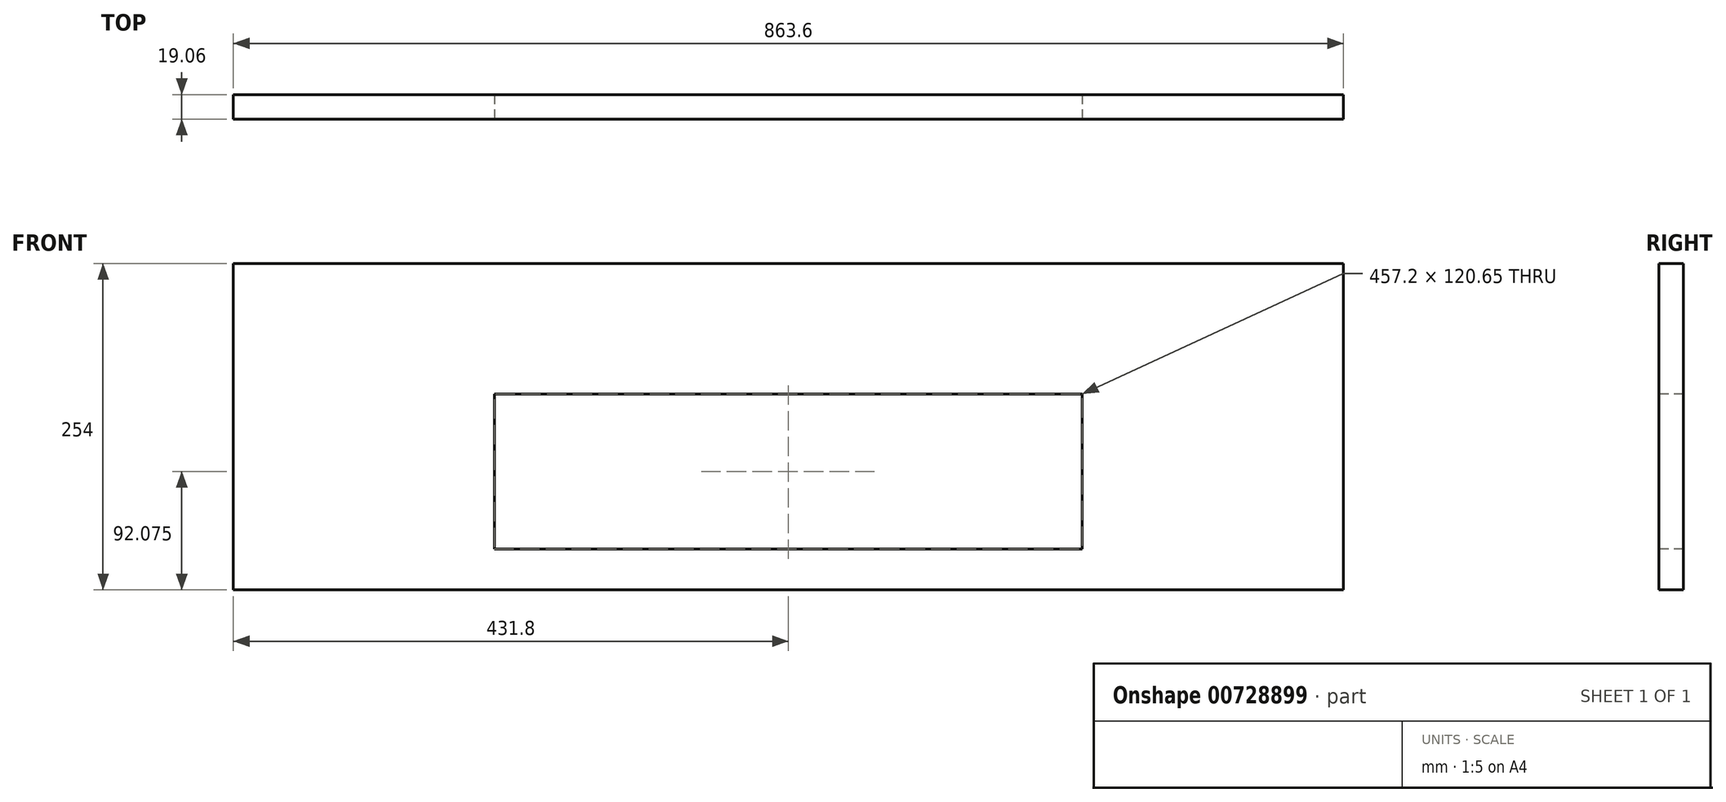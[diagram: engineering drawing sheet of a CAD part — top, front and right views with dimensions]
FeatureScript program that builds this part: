
annotation { "Feature Type Name" : "Feature", "Feature Type Description" : "" }
export const myFeature = defineFeature(function(context is Context, id is Id, definition is map)
    precondition{}
    {
        {
            var Q0;
            Q0=qCreatedBy(makeId("Right.planeOp"),FACE);
            var sketch = newSketch(context, id + "F0", { "sketchPlane" : qUnion([Q0])});
            skLineSegment(sketch, "E0.bottom", {"start": v(9.52, 127) * mm, "end": v(-9.52, 127) * mm});
            skLineSegment(sketch, "E0.top", {"start": v(9.53, -127) * mm, "end": v(-9.52, -127) * mm});
            skLineSegment(sketch, "E0.left", {"start": v(9.52, 127) * mm, "end": v(9.53, -127) * mm});
            skLineSegment(sketch, "E0.right", {"start": v(-9.52, 127) * mm, "end": v(-9.52, -127) * mm});
            skPoint(sketch, "E0.middle", {"position": v(0, 0) * mm});
            skSolve(sketch);
        }
        {
            var Q0;
            Q0=makeQuery(id+"F0.imprint","IMPRINT",FACE,{"disambiguationData":[TD([[makeQuery(id+"F0.imprint","IMPRINT",EDGE,{"derivedFrom":sQuery(id+"F0.wireOp",EDGE,"E0.bottom")}),1.0]])]});
            extrude(context, id + "F1", {"entities" : qUnion([Q0]), "oppositeDirection" : true, "depth" : 863.6 * mm, "offsetDistance" : 25.4 * mm});
        }
        {
            var Q0;
            Q0=makeQuery(id+"F1.opExtrude","SWEPT_FACE",FACE,{"disambiguationData":[OSD([sQuery(id+"F0.wireOp",EDGE,"E0.right")])]});
            var sketch = newSketch(context, id + "F2", { "sketchPlane" : qUnion([Q0])});
            skLineSegment(sketch, "E1.bottom", {"start": v(-203.2, -95.25) * mm, "end": v(-660.4, -95.25) * mm});
            skLineSegment(sketch, "E1.top", {"start": v(-203.2, 25.4) * mm, "end": v(-660.4, 25.4) * mm});
            skLineSegment(sketch, "E1.left", {"start": v(-203.2, -95.25) * mm, "end": v(-203.2, 25.4) * mm});
            skLineSegment(sketch, "E1.right", {"start": v(-660.4, -95.25) * mm, "end": v(-660.4, 25.4) * mm});
            skPoint(sketch, "E1.middle", {"position": v(-431.8, -34.92) * mm});
            skSolve(sketch);
        }
        {
            var Q0;
            Q0=makeQuery(id+"F2.imprint","IMPRINT",FACE,{"disambiguationData":[TD([[makeQuery(id+"F2.imprint","IMPRINT",EDGE,{"derivedFrom":sQuery(id+"F2.wireOp",EDGE,"E1.bottom")}),-1.0]])]});
            extrude(context, id + "F3", {"entities" : qUnion([Q0]), "operationType" : NewBodyOperationType.REMOVE, "endBound" : BoundingType.THROUGH_ALL, "oppositeDirection" : true, "depth" : 25.4 * mm, "offsetDistance" : 25.4 * mm});
        }
    });
